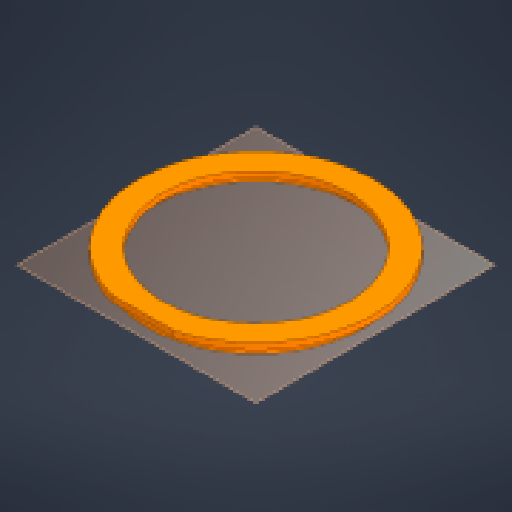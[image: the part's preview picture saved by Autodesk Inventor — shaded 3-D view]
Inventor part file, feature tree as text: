
AUTODESK INVENTOR PART (.ipt)
format: ipt  version: 2024 (Build 280153000, 153)  size: 176,640 bytes
history: native  units: mm
features: other x6, reference x5, sketch x2, extrude x2
ambient origin geometry x8: Origin, YZ Plane, XZ Plane, XY Plane, X Axis, Y Axis, Z Axis, Center Point
bodies: Body1 (feature_tree)
feature tree (15):
  other  "Твердое тело1"
  other  "РабПлоскость1"
  sketch  "Эскиз1"
  other  "РабПлоскость2"
  extrude  "Выдавливание1"  Depth=10.0mm TaperAngle=0.0deg
  extrude  "Выдавливание2"  Depth=2.0mm TaperAngle=0.0deg
  reference  "Ссылка1"
  reference  "Ссылка2"
  sketch  "Эскиз2"
  reference  "Ссылка3"
  reference  "Ссылка7"
  reference  "Ссылка9"
  parser-record x1  (decoder bookkeeping rows leaked as tree rows — omitted from the tree; the rows remain in map.json)
  other  "manipulator.iam"
  other  "platform:2"
note: 1 file-system path scrubbed to <path> (originals preserved in map.json)
